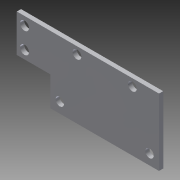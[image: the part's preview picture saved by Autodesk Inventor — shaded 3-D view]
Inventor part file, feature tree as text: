
AUTODESK INVENTOR PART (.ipt)
format: ipt  version: 2013 (Build 170138000, 138)  size: 130,560 bytes
history: native  units: in
note: dims shown in document units (in); Inventor stores cm internally (conversion verified against a paired STEP export)
features: sketch x4, reference x4, other x3, extrude x2, sheet_metal_op x1
ambient origin geometry x8: Origin, YZ Plane, XZ Plane, XY Plane, X Axis, Y Axis, Z Axis, Center Point
feature tree (14):
  sheet_metal_op  "Face2"
  sketch  "Sketch7"  dims[d3=0.295in d4=0.25in]
  extrude  "Extrusion3"  Depth=2.0in
  extrude  "Extrusion4"  Depth=0.25in
  other  "Plate5"
  sketch  "Sketch6"  dims[d1=2.244in d2=2.0in]
  reference  "Reference1"
  reference  "Reference2"
  sketch  "Sketch8"  dims[d5=0.295in]
  reference  "Reference3"
  reference  "Reference4"
  sketch  "Sketch12"  dims[d8=0.125in d19=0.25in d48=0.5in d51=2.0in d56=0.125in d57=0.5in d60=0.125in d61=0.0in d62=0.125in d63=0.0in d67=1.5in d70=1.0in d71=0.0in d72=1.0in d73=1.0in d74=0.0in]
  other  "Cut1"
  other  "Cut2"
